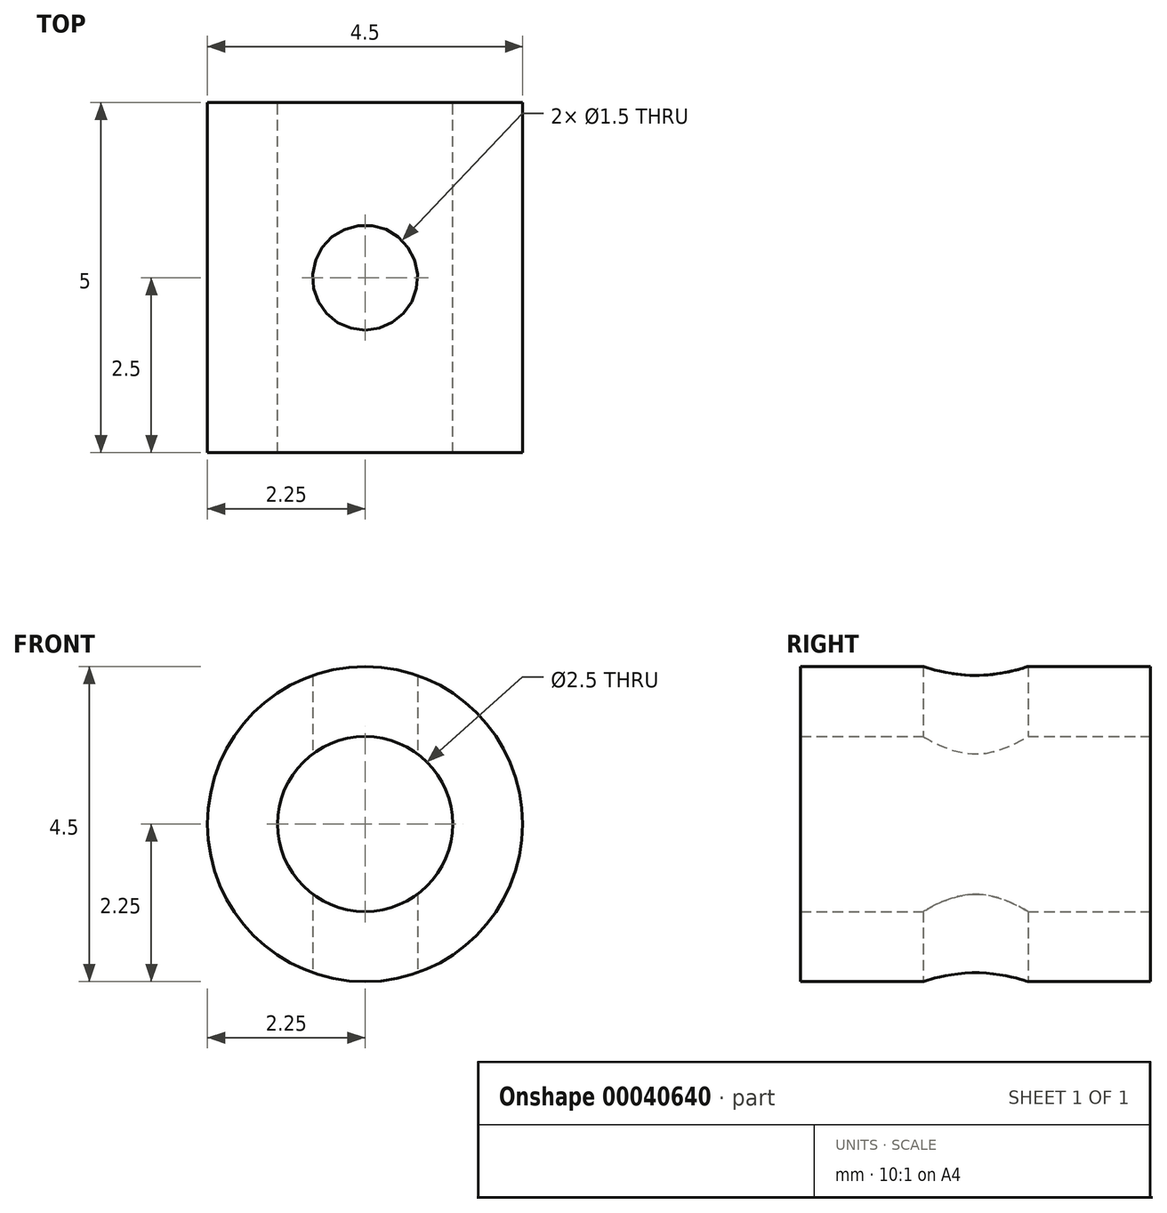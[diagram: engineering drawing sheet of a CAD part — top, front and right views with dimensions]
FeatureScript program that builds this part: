
annotation { "Feature Type Name" : "Feature", "Feature Type Description" : "" }
export const myFeature = defineFeature(function(context is Context, id is Id, definition is map)
    precondition{}
    {
        {
            var Q0;
            Q0=qCreatedBy(makeId("Top.planeOp"),FACE);
            var sketch = newSketch(context, id + "F0", { "sketchPlane" : qUnion([Q0])});
            skLineSegment(sketch, "E0", {"start": v(-50, 0) * mm, "end": v(50, 0) * mm, "construction": true});
            skLineSegment(sketch, "E1", {"start": v(0, 50) * mm, "end": v(0, -50) * mm, "construction": true});
            skSolve(sketch);
        }
        {
            var Q0;
            Q0=qCreatedBy(makeId("Front.planeOp"),FACE);
            var sketch = newSketch(context, id + "F1", { "sketchPlane" : qUnion([Q0])});
            skCircle(sketch, "E2", {"center": v(0, 0) * mm, "radius": 2.25 * mm});
            skCircle(sketch, "E3", {"center": v(0, 0) * mm, "radius": 1.25 * mm});
            skSolve(sketch);
        }
        {
            var Q0;
            Q0=qCreatedBy(makeId("Top.planeOp"),FACE);
            var sketch = newSketch(context, id + "F2", { "sketchPlane" : qUnion([Q0])});
            skCircle(sketch, "E4", {"center": v(0, 0) * mm, "radius": 0.75 * mm});
            skSolve(sketch);
        }
        {
            var Q0;
            Q0=qSketchRegion(id+"F1",true);
            extrude(context, id + "F3", {"entities" : qUnion([Q0]), "endBound" : BoundingType.SYMMETRIC, "depth" : 5 * mm});
        }
        {
            var Q0;
            Q0=qSketchRegion(id+"F2",true);
            extrude(context, id + "F4", {"entities" : qUnion([Q0]), "operationType" : NewBodyOperationType.REMOVE, "endBound" : BoundingType.THROUGH_ALL, "depth" : 25 * mm, "hasSecondDirection" : true, "secondDirectionBound" : SecondDirectionBoundingType.THROUGH_ALL, "secondDirectionOppositeDirection" : true, "secondDirectionDepth" : 25 * mm});
        }
    });
